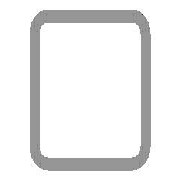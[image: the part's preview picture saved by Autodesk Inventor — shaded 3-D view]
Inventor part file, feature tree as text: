
AUTODESK INVENTOR PART (.ipt)
format: ipt  version: 2018 (Build 220112000, 112)  size: 150,016 bytes
history: native  units: mm (DEFAULTED — no unit token found)
features: other x4, sketch x4, extrude x2, plane x1
ambient origin geometry x8: Origin, YZ Plane, XZ Plane, XY Plane, X Axis, Y Axis, Z Axis, Center Point
bodies: Solid1 (feature_tree)
feature tree (11):
  other  "Tubolare horizontal 45 - Taglio"
  other  "Driven Length"
  other  "Piano iniziale"
  other  "Piano finale"
  extrude  "Corpo"  TaperAngle=0.0deg  [1 undecoded]
  extrude  "Estrusione2"  Depth=40.0mm
  sketch  "Schizzo"
  sketch  "Sketch3"  dims[d3=450.0mm d4=0.0mm]
  plane  "Work Plane3"
  sketch  "Sketch4"  dims[d7=4.0mm d9=40.0mm d11=40.0mm d12=2.0mm d13=-0.0mm d14=450.0mm d15=20.0mm d16=20.0mm d17=90.0deg d18=450.0mm d19=45.0deg d20=135.0deg d21=0.0mm d22=0.0mm]
  sketch  "Schizzo5"
note: 1 required parameter value undecoded (feature->parameter linkage not recoverable at this tier; creation-order binding heuristic only, values carry confidence <= 0.55)
